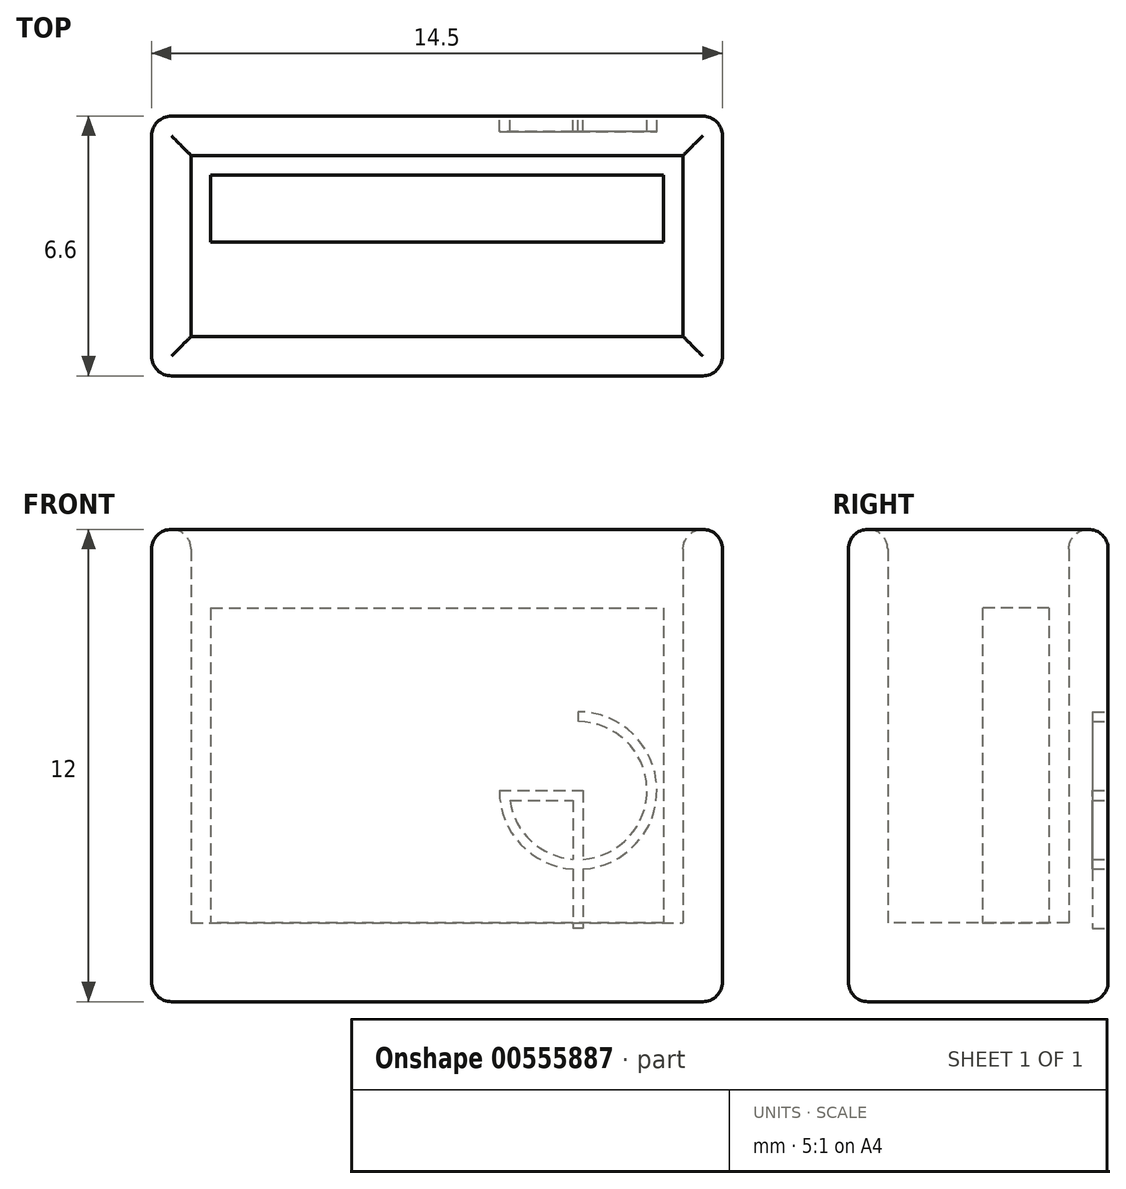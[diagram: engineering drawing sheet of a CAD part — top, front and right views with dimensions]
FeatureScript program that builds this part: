
annotation { "Feature Type Name" : "Feature", "Feature Type Description" : "" }
export const myFeature = defineFeature(function(context is Context, id is Id, definition is map)
    precondition{}
    {
        {
            var Q0;
            Q0=qCreatedBy(makeId("Top.planeOp"),FACE);
            var sketch = newSketch(context, id + "F0", { "sketchPlane" : qUnion([Q0])});
            skLineSegment(sketch, "E0.bottom", {"start": v(-5.64, 2.3) * mm, "end": v(6.86, 2.3) * mm});
            skLineSegment(sketch, "E0.top", {"start": v(-5.64, -2.3) * mm, "end": v(6.86, -2.3) * mm});
            skLineSegment(sketch, "E0.left", {"start": v(-5.64, 2.3) * mm, "end": v(-5.64, -2.3) * mm});
            skLineSegment(sketch, "E0.right", {"start": v(6.86, 2.3) * mm, "end": v(6.86, -2.3) * mm});
            skLineSegment(sketch, "E1.0", {"start": v(-6.64, -3.3) * mm, "end": v(7.86, -3.3) * mm});
            skLineSegment(sketch, "E1.1", {"start": v(-6.64, 3.3) * mm, "end": v(-6.64, -3.3) * mm});
            skLineSegment(sketch, "E1.2", {"start": v(-6.64, 3.3) * mm, "end": v(7.86, 3.3) * mm});
            skLineSegment(sketch, "E1.3", {"start": v(7.86, 3.3) * mm, "end": v(7.86, -3.3) * mm});
            skLineSegment(sketch, "E2.bottom", {"start": v(-5.14, 1.8) * mm, "end": v(6.36, 1.8) * mm});
            skLineSegment(sketch, "E2.top", {"start": v(-5.14, 0.1) * mm, "end": v(6.36, 0.1) * mm});
            skLineSegment(sketch, "E2.left", {"start": v(-5.14, 1.8) * mm, "end": v(-5.14, 0.1) * mm});
            skLineSegment(sketch, "E2.right", {"start": v(6.36, 1.8) * mm, "end": v(6.36, 0.1) * mm});
            skSolve(sketch);
        }
        {
            var Q0;
            Q0=qSketchRegion(id+"F0",true);
            extrude(context, id + "F1", {"entities" : qUnion([Q0]), "depth" : 12 * mm, "offsetDistance" : 25 * mm});
        }
        {
            var Q0;
            {var subQ0=sQuery(id+"F0.wireOp",EDGE,"E0.top");Q0=makeQuery(id+"F0.imprint","IMPRINT",FACE,{"disambiguationData":[TD([[makeQuery(id+"F0.imprint","IMPRINT",EDGE,{"derivedFrom":subQ0}),1.0]])]});}
            var Q1;
            {var subQ0=sQuery(id+"F0.wireOp",EDGE,"E0.bottom");Q1=makeQuery(id+"F0.imprint","IMPRINT",FACE,{"disambiguationData":[TD([[makeQuery(id+"F0.imprint","IMPRINT",EDGE,{"derivedFrom":subQ0}),-1.0]])]});}
            var Q2;
            Q2=makeQuery(id+"F0.imprint","IMPRINT",FACE,{"disambiguationData":[TD([[makeQuery(id+"F0.imprint","IMPRINT",EDGE,{"derivedFrom":sQuery(id+"F0.wireOp",EDGE,"E2.bottom")}),-1.0]])]});
            extrude(context, id + "F2", {"entities" : qUnion([Q0, Q1, Q2]), "operationType" : NewBodyOperationType.ADD, "depth" : 2 * mm, "offsetDistance" : 25 * mm});
        }
        {
            var Q0;
            Q0=makeQuery(id+"F0.imprint","IMPRINT",FACE,{"disambiguationData":[TD([[makeQuery(id+"F0.imprint","IMPRINT",EDGE,{"derivedFrom":sQuery(id+"F0.wireOp",EDGE,"E2.bottom")}),-1.0]])]});
            extrude(context, id + "F3", {"entities" : qUnion([Q0]), "operationType" : NewBodyOperationType.ADD, "depth" : 10 * mm, "offsetDistance" : 25 * mm});
        }
        {
            var Q0;
            Q0=makeQuery(id+"F1.opExtrude","CAP_FACE",FACE,{"disambiguationData":[OSD([sQuery(id+"F0.wireOp",EDGE,"E0.bottom"),sQuery(id+"F0.wireOp",EDGE,"E0.top"),sQuery(id+"F0.wireOp",EDGE,"E0.left"),sQuery(id+"F0.wireOp",EDGE,"E0.right"),sQuery(id+"F0.wireOp",EDGE,"E1.0"),sQuery(id+"F0.wireOp",EDGE,"E1.1"),sQuery(id+"F0.wireOp",EDGE,"E1.2"),sQuery(id+"F0.wireOp",EDGE,"E1.3")])],"isStart":false});
            var Q1;
            Q1=makeQuery(id+"F1.opExtrude","SWEPT_EDGE",EDGE,{"disambiguationData":[OSD([sQuery(id+"F0.wireOp",EDGE,"E1.2"),sQuery(id+"F0.wireOp",EDGE,"E1.3")])]});
            var Q2;
            Q2=makeQuery(id+"F1.opExtrude","SWEPT_EDGE",EDGE,{"disambiguationData":[OSD([sQuery(id+"F0.wireOp",EDGE,"E1.0"),sQuery(id+"F0.wireOp",EDGE,"E1.3")])]});
            var Q3;
            Q3=makeQuery(id+"F1.opExtrude","CAP_EDGE",EDGE,{"disambiguationData":[OSD([sQuery(id+"F0.wireOp",EDGE,"E1.3")])],"isStart":true});
            var Q4;
            Q4=makeQuery(id+"F1.opExtrude","CAP_EDGE",EDGE,{"disambiguationData":[OSD([sQuery(id+"F0.wireOp",EDGE,"E1.2")])],"isStart":true});
            var Q5;
            Q5=makeQuery(id+"F1.opExtrude","SWEPT_EDGE",EDGE,{"disambiguationData":[OSD([sQuery(id+"F0.wireOp",EDGE,"E1.1"),sQuery(id+"F0.wireOp",EDGE,"E1.2")])]});
            var Q6;
            Q6=makeQuery(id+"F1.opExtrude","SWEPT_EDGE",EDGE,{"disambiguationData":[OSD([sQuery(id+"F0.wireOp",EDGE,"E1.0"),sQuery(id+"F0.wireOp",EDGE,"E1.1")])]});
            var Q7;
            Q7=makeQuery(id+"F1.opExtrude","CAP_EDGE",EDGE,{"disambiguationData":[OSD([sQuery(id+"F0.wireOp",EDGE,"E1.0")])],"isStart":true});
            var Q8;
            Q8=makeQuery(id+"F1.opExtrude","CAP_EDGE",EDGE,{"disambiguationData":[OSD([sQuery(id+"F0.wireOp",EDGE,"E1.1")])],"isStart":true});
            fillet(context, id + "F4", {"entities" : qUnion([Q0, Q1, Q2, Q3, Q4, Q5, Q6, Q7, Q8]), "radius" : .5 * mm, "tangentPropagation" : true, "allowEdgeOverflow" : false});
        }
        {
            var Q0;
            Q0=makeQuery(id+"F1.opExtrude","SWEPT_FACE",FACE,{"disambiguationData":[OSD([sQuery(id+"F0.wireOp",EDGE,"E1.2")])]});
            var sketch = newSketch(context, id + "F5", { "sketchPlane" : qUnion([Q0])});
            skLineSegment(sketch, "E3.bottom", {"start": v(-4.2, 7.36) * mm, "end": v(-2.2, 7.36) * mm, "construction": true});
            skLineSegment(sketch, "E3.top", {"start": v(-4.2, 5.36) * mm, "end": v(-2.2, 5.36) * mm, "construction": true});
            skLineSegment(sketch, "E3.left", {"start": v(-4.2, 7.36) * mm, "end": v(-4.2, 5.36) * mm, "construction": true});
            skLineSegment(sketch, "E3.right", {"start": v(-2.2, 7.36) * mm, "end": v(-2.2, 5.36) * mm, "construction": true});
            skArc(sketch, "E4", {"start": v(-4.2, 7.36) * mm, "mid": v(-5.6, 3.95) * mm, "end": v(-2.2, 5.36) * mm});
            skLineSegment(sketch, "E5", {"start": v(-4.2, 7.36) * mm, "end": v(-4.2, 7.11) * mm});
            skLineSegment(sketch, "E6", {"start": v(-2.2, 5.36) * mm, "end": v(-2.44, 5.36) * mm});
            skArc(sketch, "E7", {"start": v(-4.2, 7.11) * mm, "mid": v(-5.43, 4.13) * mm, "end": v(-2.44, 5.36) * mm});
            skLineSegment(sketch, "E8", {"start": v(-2.44, 5.36) * mm, "end": v(-4.31, 5.36) * mm});
            skLineSegment(sketch, "E9", {"start": v(-4.31, 5.36) * mm, "end": v(-4.31, 1.86) * mm});
            skLineSegment(sketch, "E10", {"start": v(-4.31, 1.86) * mm, "end": v(-4.06, 1.86) * mm});
            skLineSegment(sketch, "E11", {"start": v(-2.46, 5.11) * mm, "end": v(-4.06, 5.11) * mm});
            skLineSegment(sketch, "E12", {"start": v(-4.06, 5.11) * mm, "end": v(-4.06, 1.86) * mm});
            skSolve(sketch);
        }
        {
            var Q0;
            Q0 = qSketchRegion(id + "F5", true);
            extrude(context, id + "F6", {"entities" : qUnion([Q0]), "operationType" : NewBodyOperationType.REMOVE, "oppositeDirection" : true, "depth" : .4 * mm, "offsetDistance" : 25 * mm});
        }
    });
